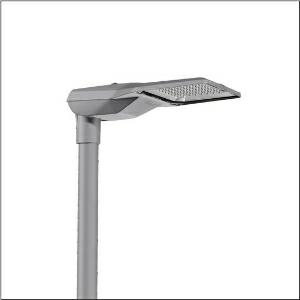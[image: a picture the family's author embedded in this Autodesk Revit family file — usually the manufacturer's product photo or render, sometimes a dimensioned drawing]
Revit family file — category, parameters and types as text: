
# Revit family: streetlight_sl_21_iq_midi___p0_8a_5xe3u31v08nb_7897
name_source: partatom
category: Lighting Fixtures
units: mm (PartAtom-declared; Revit-internal decimal feet)

## family parameters
Cut with Voids When Loaded = No
Host = Face
Light Source = No
Part Type = Normal
Room Calculation Point = No
Round Connector Dimension = Use Diameter
Shared = No

## types (1)
- --- (1 x LED, 21740 lm, 136.6 W, 3000K)
    Apparent Load = 137 VA
    CIE Flux Codes = 36 69 97 100 100
    Color Rendering = 70
    Color Temperature = 3000K
    Default Elevation = 1800 mm
    Description = Streetlight SL 21 iQ midi, mast luminaire, primary light control with lens, of PMMA, primary optical cover: cover, of toughened safety glass, transparent, light distribution: P0.8a, light emission: direct distribution, primary light characteristic: asymmetric, installation type: post-top, side-entry, LED, High Power LED, rated luminous flux: 21.740lm, luminous efficacy: 159lm/W, light colour: 730, colour temperature: 3000K, control gear: iQ-Street Remote, D4i with power reduction, control: pre-setting: logarithmic dimming characteristic, Street-Remote, Auto-Match, Temp-Guard, Lumen-Switch, Night-Set, Smart-Wire, Light-Fading, Desk-Remote (wireless, voltage-free reading and setting of iQ features in the workshop via application-optimized NFC function/RFID function), optimised constant luminous flux control (CLO 2.0), mains connection: 230..240V, AC, 50/60Hz, start of lifetime: 137W, end of service life: 144W, reduction: 61W, luminaire housing, of diecast aluminium, powder-coated, Siteco® metallic grey (DB 702S), corrosivity category C5 mid according to DIN EN ISO 12944, please order mast flange separately, inclination adjustable: 0°, 5°, 10°, 15°, sealing non-destructively replaceable, multi-level sealing system, length: 644mm, width: 335mm, height: 110mm, mast flange for spigot size: 42mm (side-entry): 5XC10008XM4, 60/48mm (side-entry/post-top): 5XC10108XM2, 76/60mm (side-entry/post-top): 5XC10108XM1, mounting height: 4..8m, Smart Interface above, protection rating (complete): IP66, insulation class (complete): insulation class II (safety insulation), certification: CE, ENEC, ENEC+, VDE, impact resistance: IK10, permissible operating ambient temperature for outdoor applications: -40..+50°C, standard-compliant lighting for roads and squares, packaging unit: 1 piece

Light Distribution: P0.8a
    Height = 111 mm
    Lamp = 1 x LED
    Lamp Light Flux = 21740 lm
    Lamp Power = 136.6 W
    Lamp count = 1
    Length = 644 mm
    Luminous efficacy = 159 lm/W
    Manufacturer = Siteco
    ModVariant = No
    Model = 5XE3U31V08NB
    Number of Poles = 1
    OnlyDefault = Yes
    Power Factor = 1
    Product Name = Streetlight SL 21 iQ midi | P0.8a
    Product group = mast luminaire | pylon top
    ProductGroupID = 6100
    Protection Class = Protection class II
    Protection Degree = IP 66
    RLX_Detail_Level = 1
    RLX_Emergency_Light_Flux = 0 lm
    RLX_Emergency_Type = 0
    RLX_Emergency_Type_DB = No
    RlxData = <blob elided: 90709 chars, md5=27a2f82b>
    Socket = socket
    Standby Power = 0 W
    System Light Flux = 21740 lm
    System Power = 137 W
    Type Comments = factory setting: luminous flux: 100 % | dim-lin: 254 | 733 mA
    Type Image = l_1004302.jpg
    URL = http://relux.com
    VarID = @adj_093545
    Voltage = 0 V
    Weight = 0.00 kg
    Width = 336 mm

## geometry (parser evidence)
native form markers: Blend x4, Sweep x10
no freeform markers — native parametric forms only
